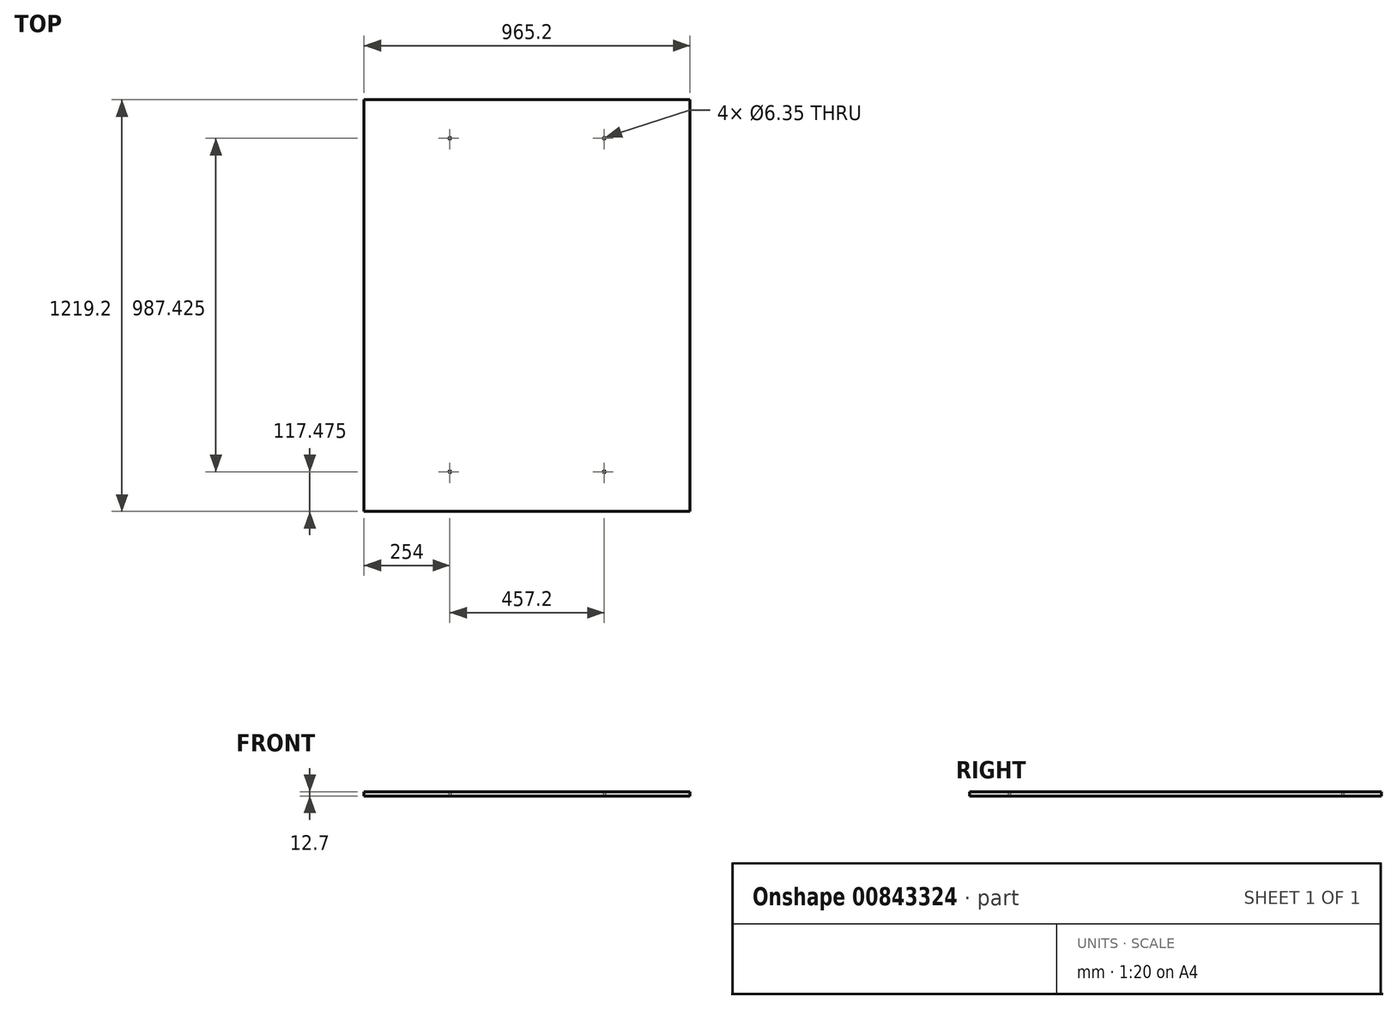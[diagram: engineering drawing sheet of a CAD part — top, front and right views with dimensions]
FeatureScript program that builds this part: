
annotation { "Feature Type Name" : "Feature", "Feature Type Description" : "" }
export const myFeature = defineFeature(function(context is Context, id is Id, definition is map)
    precondition{}
    {
        {
            var Q0;
            Q0=qCreatedBy(makeId("Top.planeOp"),FACE);
            var sketch = newSketch(context, id + "F0", { "sketchPlane" : qUnion([Q0])});
            skLineSegment(sketch, "E0.bottom", {"start": v(482.6, -609.6) * mm, "end": v(-482.6, -609.6) * mm});
            skLineSegment(sketch, "E0.top", {"start": v(482.6, 609.6) * mm, "end": v(-482.6, 609.6) * mm});
            skLineSegment(sketch, "E0.left", {"start": v(482.6, -609.6) * mm, "end": v(482.6, 609.6) * mm});
            skLineSegment(sketch, "E0.right", {"start": v(-482.6, -609.6) * mm, "end": v(-482.6, 609.6) * mm});
            skPoint(sketch, "E0.middle", {"position": v(0, 0) * mm});
            skSolve(sketch);
        }
        {
            var Q0;
            Q0 = qSketchRegion(id + "F0", true);
            extrude(context, id + "F1", {"entities" : qUnion([Q0]), "depth" : 12.7 * mm, "offsetDistance" : 25.4 * mm});
        }
        {
            var Q0;
            Q0=qCreatedBy(makeId("Top.planeOp"),FACE);
            var sketch = newSketch(context, id + "F2", { "sketchPlane" : qUnion([Q0])});
            skLineSegment(sketch, "E1", {"start": v(-397.5, -492.13) * mm, "end": v(17.3, -492.13) * mm, "construction": true});
            skCircle(sketch, "E2", {"center": v(-228.6, -492.13) * mm, "radius": 3.17 * mm});
            skCircle(sketch, "E3", {"center": v(228.6, -492.12) * mm, "radius": 3.17 * mm});
            skSolve(sketch);
        }
        {
            var Q0;
            Q0 = qSketchRegion(id + "F2", true);
            extrude(context, id + "F3", {"entities" : qUnion([Q0]), "operationType" : NewBodyOperationType.REMOVE, "depth" : 25.4 * mm, "offsetDistance" : 25.4 * mm});
        }
        {
            var Q0;
            Q0=qCreatedBy(makeId("Top.planeOp"),FACE);
            var sketch = newSketch(context, id + "F4", { "sketchPlane" : qUnion([Q0])});
            skLineSegment(sketch, "E4.0", {"start": v(482.6, 495.3) * mm, "end": v(-482.6, 495.3) * mm, "construction": true});
            skCircle(sketch, "E5", {"center": v(-228.6, 495.3) * mm, "radius": 3.17 * mm});
            skCircle(sketch, "E6", {"center": v(228.6, 495.3) * mm, "radius": 3.17 * mm});
            skSolve(sketch);
        }
        {
            var Q0;
            Q0 = qSketchRegion(id + "F4", true);
            extrude(context, id + "F5", {"entities" : qUnion([Q0]), "operationType" : NewBodyOperationType.REMOVE, "depth" : 25.4 * mm, "offsetDistance" : 25.4 * mm});
        }
    });
